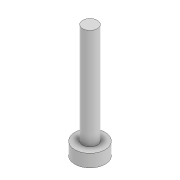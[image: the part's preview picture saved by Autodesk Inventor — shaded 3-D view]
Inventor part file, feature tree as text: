
AUTODESK INVENTOR PART (.ipt)
format: ipt  version: 2022 (Build 260153000, 153)  size: 83,968 bytes
history: native  units: mm
features: extrude x2, sketch x2
ambient origin geometry x8: Origin, YZ Plane, XZ Plane, XY Plane, X Axis, Y Axis, Z Axis, Center Point
bodies: Solid1 (feature_tree)
feature tree (4):
  extrude  "Extrusion1"  Depth=2.5mm TaperAngle=0.0deg
  extrude  "Extrusion2"  Depth=20.0mm TaperAngle=0.0deg
  sketch  "Sketch1"  dims[d0=6.0mm d1=2.5mm d2=0.0mm]
  sketch  "Sketch2"  dims[d3=2.9mm d4=20.0mm d5=0.0mm]
